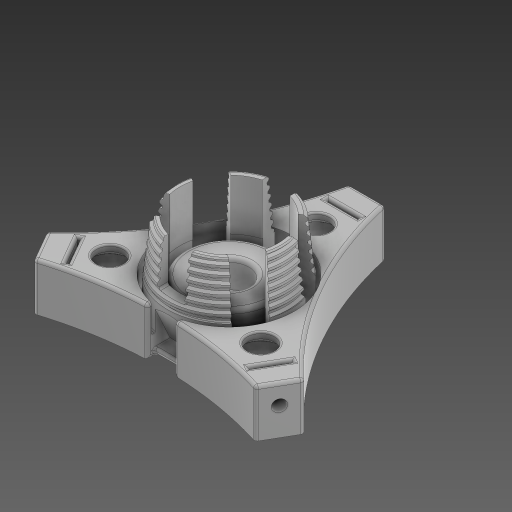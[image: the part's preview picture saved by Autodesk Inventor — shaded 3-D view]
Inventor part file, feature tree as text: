
AUTODESK INVENTOR PART (.ipt)
format: ipt  version: 2024 (Build 280153000, 153)  size: 1,769,984 bytes
history: native  units: mm
features: sketch x18, extrude x13, fillet x10, chamfer x4, hole x3, pattern_circular x3, draft x2, helix x2, plane x2, projected_geometry x2
ambient origin geometry x8: Origin, YZ Plane, XZ Plane, XY Plane, X Axis, Y Axis, Z Axis, Center Point
bodies: Solid1 (feature_tree)
feature tree (59):
  extrude  "Extrusion1"  Depth=29.5mm
  draft  "FaceDraft1"
  sketch  "Sketch2"  dims[d7=6.806784mm d8=0.55605mm]
  helix  "Coil1"  [1 undecoded]
  helix  "Coil2"  [1 undecoded]
  extrude  "Extrusion2"  Depth=0.55605mm
  extrude  "Extrusion3"  TaperAngle=0.0deg  [1 undecoded]
  fillet  "Fillet1"  [1 undecoded]
  chamfer  "Chamfer1"  Distance=0.3mm Angle=45.0deg
  plane  "Work Plane1"
  extrude  "Extrusion4"  TaperAngle=0.0deg  [1 undecoded]
  extrude  "Extrusion8"  Depth=60.0mm TaperAngle=360.0deg
  hole  "Hole2"  [1 undecoded]
  sketch  "Sketch13"  dims[d58=6.0mm d65=60.0mm d67=360.0deg]
  extrude  "Extrusion11"  Depth=10.0mm TaperAngle=0.0deg
  hole  "Bearing Hole"  [1 undecoded]
  pattern_circular  "Circular Pattern4"  Count=3 Angle=360.0deg
  extrude  "Extrusion13"  Depth=7.0mm TaperAngle=0.0deg
  sketch  "Sketch20"  dims[d126=6.804mm d127=6.0mm d128=9.979mm d129=8.89mm d130=90.0deg d131=8.0mm d132=20.594885mm d133=22.0mm d134=30.0mm d135=360.0deg]
  extrude  "Extrusion14"  Depth=1.55mm TaperAngle=45.0deg
  sketch  "Sketch18"  dims[d124=34.0mm]
  fillet  "Fillet9"  Radius=0.24mm
  chamfer  "Chamfer4"  [1 undecoded]
  chamfer  "Chamfer5"  Distance=2.0mm
  fillet  "Fillet11"  Radius=34.767mm
  draft  "FaceDraft2"
  fillet  "Fillet13"  Radius=9.0mm
  extrude  "Extrusion15"  TaperAngle=30.0deg  [1 undecoded]
  hole  "Hole5"  [1 undecoded]
  pattern_circular  "Circular Pattern5"  [2 undecoded]
  plane  "Work Plane4"
  extrude  "Extrusion16"  Depth=0.75mm TaperAngle=360.0deg
  fillet  "Fillet14"  Radius=16.0mm
  fillet  "Fillet16"  [1 undecoded]
  extrude  "Extrusion17"  Depth=0.75mm
  extrude  "Extrusion19"  Depth=0.75mm
  fillet  "Fillet17"  Radius=25.0mm
  fillet  "Fillet18"  Radius=22.0mm
  fillet  "Fillet19"  Radius=31.0mm
  extrude  "Extrusion20"  Depth=0.75mm TaperAngle=0.0deg
  fillet  "Fillet20"  Radius=32.8mm
  chamfer  "Chamfer6"  Distance=9.0mm
  pattern_circular  "Circular Pattern6"  [2 undecoded]
  sketch  "Sketch1"  dims[d0=24.7mm d1=29.5mm d2=12.875mm d3=0.0mm d4=1.047198mm]
  projected_geometry  "Projected Loop1"
  sketch  "Sketch3"  dims[d9=6.806784mm]
  sketch  "Sketch4"  dims[d10=2.0mm d11=10.0mm d12=70.0mm d13=-1.047198mm d14=90.0deg d15=90.0deg d16=0.0mm d17=0.0mm d18=0.6mm]
  sketch  "Sketch5"  dims[d19=2.0mm d20=10.0mm d21=10.0mm d22=1.047198mm d23=90.0deg d24=90.0deg d25=0.0mm d26=0.0mm d27=0.0mm d28=0.0mm d29=0.0mm d30=0.0mm]
  sketch  "Sketch10"  dims[d31=0.6mm d32=0.3mm d33=2.0mm d34=45.0deg]
  sketch  "Sketch11"  dims[d36=-2.0mm d42=0.0mm d43=0.0mm]
  sketch  "Sketch15"  dims[d91=33.0mm d92=12.0mm d93=0.0mm]
  sketch  "Sketch17"  dims[d94=5.3mm d95=6.0mm d96=10.0mm d97=7.0mm d98=90.0deg d99=8.0mm d100=20.594885mm d122=10.0mm d123=0.0mm]
  sketch  "Sketch21"  dims[d146=11.34464mm d147=7.0mm d148=0.0mm]
  sketch  "Sketch22"  dims[d150=1.0mm d151=1.55mm d152=2.0mm d153=45.0deg]
  sketch  "Sketch25"  dims[d154=0.5mm d155=2.0mm d156=45.0deg d158=0.24mm]
  sketch  "Sketch26"  dims[d160=1.25mm d161=0.0mm d162=0.0mm]
  sketch  "Sketch28"  dims[d163=30.0deg]
  sketch  "Sketch29"  dims[d164=0.5mm d165=2.0mm d166=34.767mm d167=9.0mm d168=30.0deg d169=7.0mm d170=0.0mm d171=3.0mm d172=6.0mm d173=9.779mm d174=7.62mm d175=90.0deg d176=7.0mm d177=0.0mm d178=5.0mm d179=30.0mm d180=360.0deg d182=16.0mm d183=0.0mm d184=0.0mm d185=0.75mm d187=0.4mm d188=25.0mm d189=22.0mm d190=31.0mm d191=7.0mm d192=0.0mm d193=32.8mm d208=9.0mm d209=0.0mm d210=1.0mm d211=0.25mm d212=0.5mm d213=7.0mm d214=60.0mm d216=360.0deg d218=8.0mm d219=6.0mm d220=0.6mm d221=0.3mm d222=0.0mm d223=0.0mm d224=0.75mm d225=0.75mm d226=2.0mm d227=45.0deg d228=30.0mm d229=360.0deg]
  projected_geometry  "Project Cut Edges3"
note: 15 required parameter values undecoded (feature->parameter linkage not recoverable at this tier; creation-order binding heuristic only, values carry confidence <= 0.55)
